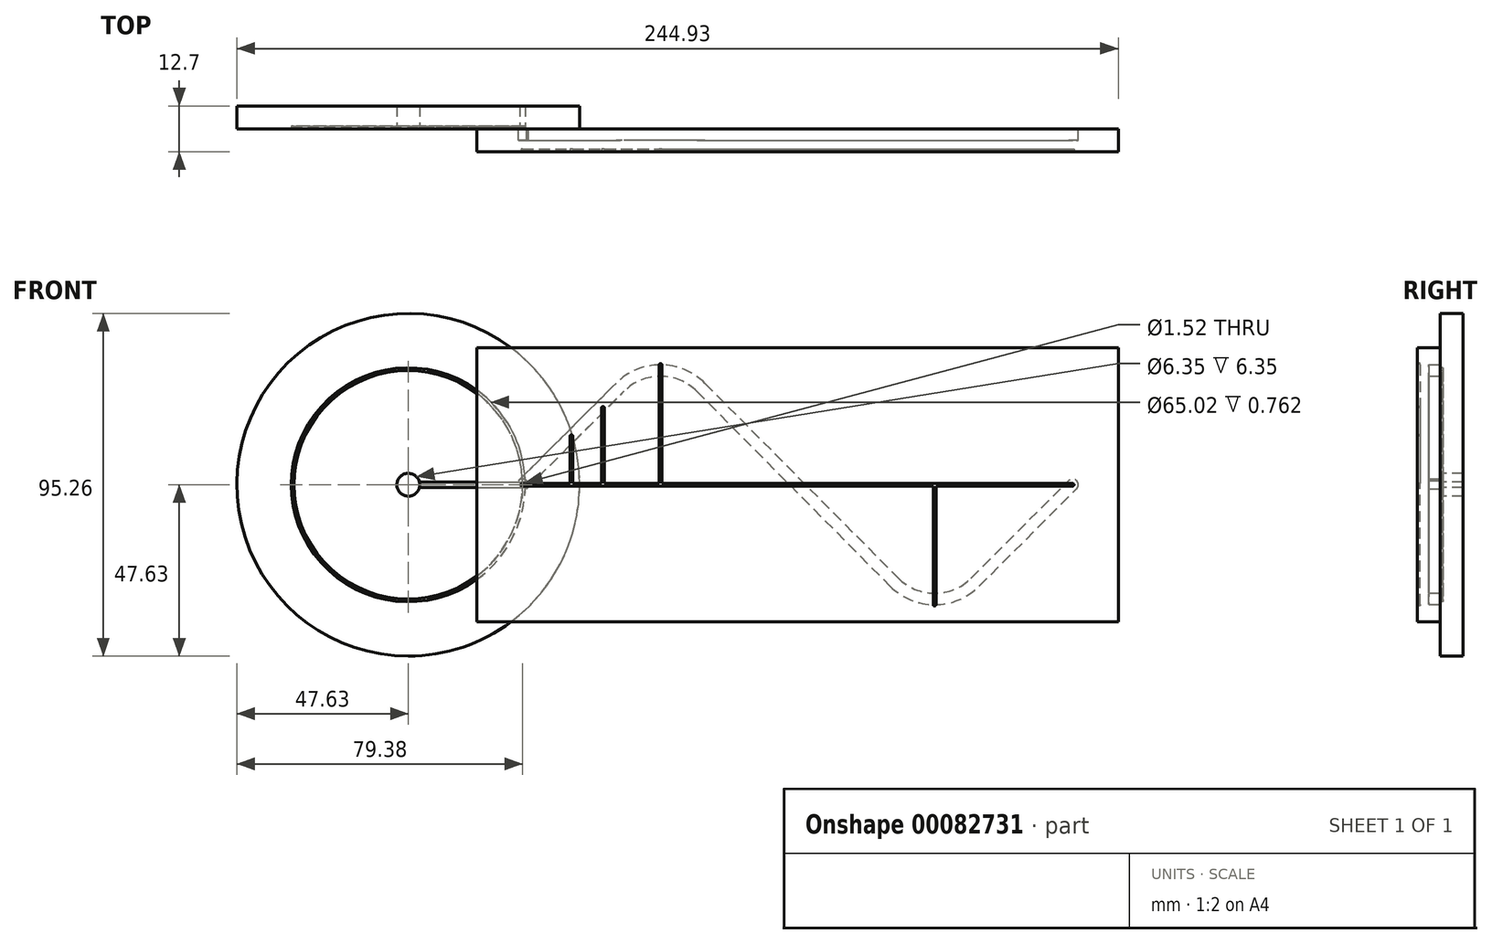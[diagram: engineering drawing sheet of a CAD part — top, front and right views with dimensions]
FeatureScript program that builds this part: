
annotation { "Feature Type Name" : "Feature", "Feature Type Description" : "" }
export const myFeature = defineFeature(function(context is Context, id is Id, definition is map)
    precondition{}
    {
        {
            var Q0;
            Q0=qCreatedBy(makeId("Front.planeOp"),FACE);
            var sketch = newSketch(context, id + "F0", { "sketchPlane" : qUnion([Q0])});
            skLineSegment(sketch, "E0.bottom", {"start": v(-12.7, -38.1) * mm, "end": v(165.55, -38.1) * mm});
            skLineSegment(sketch, "E0.top", {"start": v(-12.7, 38.1) * mm, "end": v(165.55, 38.1) * mm});
            skLineSegment(sketch, "E0.left", {"start": v(-12.7, -38.1) * mm, "end": v(-12.7, 38.1) * mm});
            skLineSegment(sketch, "E0.right", {"start": v(165.55, -38.1) * mm, "end": v(165.55, 38.1) * mm});
            skLineSegment(sketch, "E1", {"start": v(-12.7, 0) * mm, "end": v(0, 0) * mm, "construction": true});
            skLineSegment(sketch, "E2", {"start": v(0, 0) * mm, "end": v(27.1, 27.1) * mm, "construction": true});
            skLineSegment(sketch, "E3", {"start": v(49.6, 27.05) * mm, "end": v(103.25, -27.05) * mm, "construction": true});
            skLineSegment(sketch, "E4", {"start": v(125.75, -27.1) * mm, "end": v(152.85, 0) * mm, "construction": true});
            skLineSegment(sketch, "E5", {"start": v(152.85, 0) * mm, "end": v(0, 0) * mm, "construction": true});
            skPoint(sketch, "E6.visualSharp", {"position": v(38.37, 38.37) * mm});
            skArc(sketch, "E6.filletArc", {"start": v(49.6, 27.05) * mm, "mid": v(38.36, 31.75) * mm, "end": v(27.1, 27.1) * mm, "construction": true});
            skPoint(sketch, "E7.visualSharp", {"position": v(114.48, -38.37) * mm});
            skArc(sketch, "E7.filletArc", {"start": v(103.25, -27.05) * mm, "mid": v(114.5, -31.75) * mm, "end": v(125.75, -27.1) * mm, "construction": true});
            skLineSegment(sketch, "E8", {"start": v(76.43, 0) * mm, "end": v(76.43, -38.1) * mm, "construction": true});
            skLineSegment(sketch, "E9.0", {"start": v(126.87, -28.22) * mm, "end": v(153.97, -1.12) * mm});
            skLineSegment(sketch, "E9.1", {"start": v(1.12, -1.12) * mm, "end": v(28.22, 25.98) * mm});
            skArc(sketch, "E9.2", {"start": v(48.47, 25.94) * mm, "mid": v(38.36, 30.16) * mm, "end": v(28.22, 25.98) * mm});
            skLineSegment(sketch, "E9.3", {"start": v(48.47, 25.94) * mm, "end": v(102.13, -28.17) * mm});
            skArc(sketch, "E9.4", {"start": v(102.13, -28.17) * mm, "mid": v(114.49, -33.34) * mm, "end": v(126.87, -28.22) * mm});
            skLineSegment(sketch, "E10.0", {"start": v(124.63, -25.98) * mm, "end": v(151.73, 1.12) * mm});
            skLineSegment(sketch, "E10.1", {"start": v(-1.12, 1.12) * mm, "end": v(25.98, 28.22) * mm});
            skArc(sketch, "E10.2", {"start": v(50.73, 28.17) * mm, "mid": v(38.36, 33.34) * mm, "end": v(25.98, 28.22) * mm});
            skLineSegment(sketch, "E10.3", {"start": v(50.73, 28.17) * mm, "end": v(104.38, -25.94) * mm});
            skArc(sketch, "E10.4", {"start": v(104.38, -25.94) * mm, "mid": v(114.5, -30.16) * mm, "end": v(124.63, -25.98) * mm});
            skArc(sketch, "E11", {"start": v(-1.12, 1.12) * mm, "mid": v(-1.12, -1.12) * mm, "end": v(1.12, -1.12) * mm});
            skArc(sketch, "E12", {"start": v(153.97, -1.12) * mm, "mid": v(153.97, 1.12) * mm, "end": v(151.73, 1.12) * mm});
            skSolve(sketch);
        }
        {
            var Q0;
            Q0=makeQuery(id+"F0.imprint","IMPRINT",FACE,{"disambiguationData":[TD([[makeQuery(id+"F0.imprint","IMPRINT",EDGE,{"derivedFrom":sQuery(id+"F0.wireOp",EDGE,"E0.bottom")}),1.0]])]});
            extrude(context, id + "F1", {"entities" : qUnion([Q0]), "depth" : 3.17 * mm});
        }
        {
            var Q0;
            Q0=qCreatedBy(makeId("Front.planeOp"),FACE);
            var sketch = newSketch(context, id + "F2", { "sketchPlane" : qUnion([Q0])});
            skCircle(sketch, "E13", {"center": v(-31.75, 0) * mm, "radius": 31.75 * mm, "construction": true});
            skCircle(sketch, "E14", {"center": v(-31.75, 0) * mm, "radius": 47.63 * mm});
            skCircle(sketch, "E15", {"center": v(0, 0) * mm, "radius": 0.76 * mm});
            skCircle(sketch, "E16", {"center": v(-31.75, 0) * mm, "radius": 3.18 * mm});
            skSolve(sketch);
        }
        {
            var Q0;
            Q0 = qSketchRegion(id + "F2", true);
            extrude(context, id + "F3", {"entities" : qUnion([Q0]), "oppositeDirection" : true, "depth" : 6.35 * mm});
        }
        {
            var Q0;
            Q0=makeQuery(id+"F3.opExtrude","CAP_FACE",FACE,{"disambiguationData":[OSD([sQuery(id+"F2.wireOp",EDGE,"E14"),sQuery(id+"F2.wireOp",EDGE,"E15"),sQuery(id+"F2.wireOp",EDGE,"E16")])],"isStart":true});
            var sketch = newSketch(context, id + "F4", { "sketchPlane" : qUnion([Q0])});
            skArc(sketch, "E17", {"start": v(0, 0.76) * mm, "mid": v(-63.5, 0) * mm, "end": v(0, -0.76) * mm});
            skCircle(sketch, "E18.0", {"center": v(-31.75, 0) * mm, "radius": 32.51 * mm});
            skLineSegment(sketch, "E19", {"start": v(-31.75, 0) * mm, "end": v(0, 0) * mm});
            skArc(sketch, "E20.0.startCap", {"start": v(-31.75, -0.76) * mm, "mid": v(-32.51, 0) * mm, "end": v(-31.75, 0.76) * mm});
            skLineSegment(sketch, "E20.0.left", {"start": v(-31.75, 0.76) * mm, "end": v(0, 0.76) * mm});
            skLineSegment(sketch, "E20.0.right", {"start": v(-31.75, -0.76) * mm, "end": v(0, -0.76) * mm});
            skSolve(sketch);
        }
        {
            var Q0;
            Q0 = qSketchRegion(id + "F4", true);
            extrude(context, id + "F5", {"entities" : qUnion([Q0]), "operationType" : NewBodyOperationType.REMOVE, "oppositeDirection" : true, "depth" : 0.76 * mm});
        }
        {
            var Q0;
            {var subQ0=sQuery(id+"F2.wireOp",EDGE,"E14");Q0=makeQuery(id+"F5.boolean.opBoolean","SPLIT",FACE,{"disambiguationData":[TD([makeQuery(id+"F3.opExtrude","SWEPT_FACE",FACE,{"disambiguationData":[OSD([subQ0])]})])],"derivedFrom":makeQuery(id+"F3.opExtrude","CAP_FACE",FACE,{"disambiguationData":[OSD([subQ0,sQuery(id+"F2.wireOp",EDGE,"E15"),sQuery(id+"F2.wireOp",EDGE,"E16")])],"isStart":true})});}
            var sketch = newSketch(context, id + "F6", { "sketchPlane" : qUnion([Q0])});
            skCircle(sketch, "E21", {"center": v(0, 0) * mm, "radius": 1.59 * mm});
            skSolve(sketch);
        }
        {
            var Q0;
            Q0 = qSketchRegion(id + "F6", true);
            extrude(context, id + "F7", {"entities" : qUnion([Q0]), "operationType" : NewBodyOperationType.ADD, "depth" : 3.17 * mm});
        }
        {
            var Q0;
            Q0=makeQuery(id+"F1.opExtrude","CAP_FACE",FACE,{"disambiguationData":[OSD([sQuery(id+"F0.wireOp",EDGE,"E0.bottom"),sQuery(id+"F0.wireOp",EDGE,"E0.top"),sQuery(id+"F0.wireOp",EDGE,"E0.left"),sQuery(id+"F0.wireOp",EDGE,"E0.right"),sQuery(id+"F0.wireOp",EDGE,"E9.0"),sQuery(id+"F0.wireOp",EDGE,"E9.1"),sQuery(id+"F0.wireOp",EDGE,"E9.2"),sQuery(id+"F0.wireOp",EDGE,"E9.3"),sQuery(id+"F0.wireOp",EDGE,"E9.4"),sQuery(id+"F0.wireOp",EDGE,"E10.0"),sQuery(id+"F0.wireOp",EDGE,"E10.1"),sQuery(id+"F0.wireOp",EDGE,"E10.2"),sQuery(id+"F0.wireOp",EDGE,"E10.3"),sQuery(id+"F0.wireOp",EDGE,"E10.4"),sQuery(id+"F0.wireOp",EDGE,"E11"),sQuery(id+"F0.wireOp",EDGE,"E12")])],"isStart":false});
            var sketch = newSketch(context, id + "F8", { "sketchPlane" : qUnion([Q0])});
            skLineSegment(sketch, "E22.bottom", {"start": v(165.55, 38.1) * mm, "end": v(-12.7, 38.1) * mm});
            skLineSegment(sketch, "E22.top", {"start": v(165.55, -38.1) * mm, "end": v(-12.7, -38.1) * mm});
            skLineSegment(sketch, "E22.left", {"start": v(-12.7, 38.1) * mm, "end": v(-12.7, -38.1) * mm});
            skLineSegment(sketch, "E22.right", {"start": v(165.55, 38.1) * mm, "end": v(165.55, -38.1) * mm});
            skSolve(sketch);
        }
        {
            var Q0;
            Q0 = qSketchRegion(id + "F8", true);
            extrude(context, id + "F9", {"entities" : qUnion([Q0]), "operationType" : NewBodyOperationType.ADD, "depth" : 3.17 * mm});
        }
        {
            var Q0;
            Q0=makeQuery(id+"F9.opExtrude","CAP_FACE",FACE,{"disambiguationData":[OSD([sQuery(id+"F8.wireOp",EDGE,"E22.bottom"),sQuery(id+"F8.wireOp",EDGE,"E22.top"),sQuery(id+"F8.wireOp",EDGE,"E22.left"),sQuery(id+"F8.wireOp",EDGE,"E22.right")])],"isStart":false});
            var sketch = newSketch(context, id + "F10", { "sketchPlane" : qUnion([Q0])});
            skLineSegment(sketch, "E23", {"start": v(0, 0) * mm, "end": v(152.85, 0) * mm, "construction": true});
            skLineSegment(sketch, "E24", {"start": v(38.36, 33.34) * mm, "end": v(38.36, 0) * mm, "construction": true});
            skLineSegment(sketch, "E25", {"start": v(114.49, -33.34) * mm, "end": v(114.49, 0) * mm, "construction": true});
            skLineSegment(sketch, "E26", {"start": v(22.34, 21.4) * mm, "end": v(22.34, 0) * mm, "construction": true});
            skLineSegment(sketch, "E27", {"start": v(13.6, 13.52) * mm, "end": v(13.6, 0) * mm, "construction": true});
            skArc(sketch, "E28.0.startCap", {"start": v(0, -0.38) * mm, "mid": v(-0.38, 0) * mm, "end": v(0, 0.38) * mm});
            skArc(sketch, "E28.0.endCap", {"start": v(152.85, 0.38) * mm, "mid": v(153.23, 0) * mm, "end": v(152.85, -0.38) * mm});
            skLineSegment(sketch, "E28.0.left", {"start": v(0, 0.38) * mm, "end": v(13.22, 0.38) * mm});
            skLineSegment(sketch, "E28.0.right", {"start": v(0, -0.38) * mm, "end": v(114.1, -0.38) * mm});
            skArc(sketch, "E28.1.startCap", {"start": v(37.98, 33.34) * mm, "mid": v(38.36, 33.72) * mm, "end": v(38.74, 33.34) * mm});
            skArc(sketch, "E28.1.endCap", {"start": v(38.74, 0) * mm, "mid": v(38.36, -0.38) * mm, "end": v(37.98, 0) * mm});
            skLineSegment(sketch, "E28.1.left", {"start": v(38.74, 33.34) * mm, "end": v(38.74, 0.38) * mm});
            skLineSegment(sketch, "E28.1.right", {"start": v(37.98, 33.34) * mm, "end": v(37.98, 0.38) * mm});
            skArc(sketch, "E28.2.startCap", {"start": v(21.96, 21.4) * mm, "mid": v(22.34, 21.77) * mm, "end": v(22.72, 21.4) * mm});
            skArc(sketch, "E28.2.endCap", {"start": v(22.72, 0) * mm, "mid": v(22.34, -0.38) * mm, "end": v(21.96, 0) * mm});
            skLineSegment(sketch, "E28.2.left", {"start": v(22.72, 21.4) * mm, "end": v(22.72, 0.38) * mm});
            skLineSegment(sketch, "E28.2.right", {"start": v(21.96, 21.4) * mm, "end": v(21.96, 0.38) * mm});
            skArc(sketch, "E28.3.startCap", {"start": v(13.22, 13.52) * mm, "mid": v(13.6, 13.9) * mm, "end": v(13.98, 13.52) * mm});
            skArc(sketch, "E28.3.endCap", {"start": v(13.98, 0) * mm, "mid": v(13.6, -0.38) * mm, "end": v(13.22, 0) * mm});
            skLineSegment(sketch, "E28.3.left", {"start": v(13.98, 13.52) * mm, "end": v(13.98, 0.38) * mm});
            skLineSegment(sketch, "E28.3.right", {"start": v(13.22, 13.52) * mm, "end": v(13.22, 0.38) * mm});
            skArc(sketch, "E28.4.startCap", {"start": v(114.87, -33.34) * mm, "mid": v(114.49, -33.72) * mm, "end": v(114.1, -33.34) * mm});
            skArc(sketch, "E28.4.endCap", {"start": v(114.1, 0) * mm, "mid": v(114.49, 0.38) * mm, "end": v(114.87, 0) * mm, "construction": true});
            skLineSegment(sketch, "E28.4.left", {"start": v(114.1, -33.34) * mm, "end": v(114.1, -0.38) * mm});
            skLineSegment(sketch, "E28.4.right", {"start": v(114.87, -33.34) * mm, "end": v(114.87, -0.38) * mm});
            skLineSegment(sketch, "E29.trimOffspring", {"start": v(13.98, 0.38) * mm, "end": v(21.96, 0.38) * mm});
            skLineSegment(sketch, "E30.trimOffspring", {"start": v(38.74, 0.38) * mm, "end": v(152.85, 0.38) * mm});
            skLineSegment(sketch, "E31.trimOffspring", {"start": v(22.72, 0.38) * mm, "end": v(37.98, 0.38) * mm});
            skLineSegment(sketch, "E32.trimOffspring", {"start": v(114.87, -0.38) * mm, "end": v(152.85, -0.38) * mm});
            skSolve(sketch);
        }
        {
            var Q0;
            Q0 = qSketchRegion(id + "F10", true);
            extrude(context, id + "F11", {"entities" : qUnion([Q0]), "operationType" : NewBodyOperationType.REMOVE, "oppositeDirection" : true, "depth" : 0.76 * mm});
        }
    });
